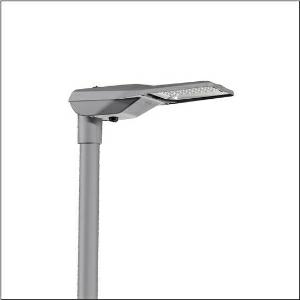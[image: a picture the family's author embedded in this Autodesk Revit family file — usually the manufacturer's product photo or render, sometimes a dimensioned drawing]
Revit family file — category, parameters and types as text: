
# Revit family: streetlight_sl_21_iq_mini___p0_8ab_5xe2r31y08hb_a9b9
name_source: partatom
category: Lighting Fixtures
units: mm (PartAtom-declared; Revit-internal decimal feet)

## family parameters
Cut with Voids When Loaded = No
Host = Face
Light Source = No
Part Type = Normal
Room Calculation Point = No
Round Connector Dimension = Use Diameter
Shared = No

## types (1)
- --- (1 x LED, 8460 lm, 71 W, 3000K)
    Apparent Load = 71 VA
    CIE Flux Codes = 36 71 98 100 100
    Color Rendering = 70
    Color Temperature = 3000K
    Default Elevation = 1800 mm
    Description = Streetlight SL 21 iQ mini, mast luminaire, primary light control with lens, of PMMA, primary optical cover: cover, of toughened safety glass, transparent, light distribution: P0.8aB, light emission: direct distribution, primary light characteristic: asymmetric, installation type: post-top, side-entry, LED, High Power LED, rated luminous flux: 8.460lm, luminous efficacy: 119lm/W, light colour: 730, colour temperature: 3000K, control gear: iQ-Street Remote, D4i with power reduction, control: pre-setting: logarithmic dimming characteristic, Street-Remote, Auto-Match, Temp-Guard, Lumen-Switch, Night-Set, Smart-Wire, Light-Fading, Desk-Remote (wireless, voltage-free reading and setting of iQ features in the workshop via application-optimized NFC function/RFID function), optimised constant luminous flux control (CLO 2.0), mains connection: 220..240V, AC, 50/60Hz, start of lifetime: 71W, end of service life: 75W, reduction: 30W, luminaire housing, of diecast aluminium, powder-coated, SITECO metallic grey (DB 702S), corrosivity category C5 high according to DIN EN ISO 12944, please order mast flange separately, inclination adjustable: 0°, 5°, 10°, 15°, sealing non-destructively replaceable, multi-level sealing system, length: 628mm, width: 235mm, height: 110mm, mast flange for spigot size: 42mm (side-entry): 5XC10008XM4, 60/48mm (side-entry/post-top): 5XC10108XM2, 76/60mm (side-entry/post-top): 5XC10108XM1, mounting height: 4..8m, Smart Interface below and above, protection rating (complete): IP66, insulation class (complete): insulation class II (safety insulation), certification: CE, ENEC, ENEC+, VDE, impact resistance: IK10, permissible operating ambient temperature for outdoor applications: -40..+50°C, standard-compliant lighting for roads and squares, packaging unit: 1 piece

Light Distribution: P0.8aB
    Height = 110 mm
    Lamp = 1 x LED
    Lamp Light Flux = 8460 lm
    Lamp Power = 71 W
    Lamp count = 1
    Length = 625 mm
    Luminous efficacy = 119 lm/W
    Manufacturer = Siteco
    ModVariant = No
    Model = 5XE2R31Y08HB
    Number of Poles = 1
    OnlyDefault = Yes
    Power Factor = 1
    Product Name = Streetlight SL 21 iQ mini | P0.8aB
    Product group = mast luminaire | pylon top
    ProductGroupID = 6100
    Protection Class = Protection class II
    Protection Degree = IP 66
    RLX_Detail_Level = 1
    RLX_Emergency_Light_Flux = 0 lm
    RLX_Emergency_Type = 0
    RLX_Emergency_Type_DB = No
    RlxData = <blob elided: 92041 chars, md5=348abe3b>
    Socket = socket
    Standby Power = 0 W
    System Light Flux = 8460 lm
    System Power = 71 W
    Type Comments = factory setting: luminous flux: 100 % | dim-lin: 254 | 716 mA
    Type Image = l_1003514.jpg
    URL = http://relux.com
    VarID = @adj_083051
    Voltage = 0 V
    Weight = 0.00 kg
    Width = 234 mm

## geometry (parser evidence)
native form markers: Blend x4, Sweep x11
no freeform markers — native parametric forms only
